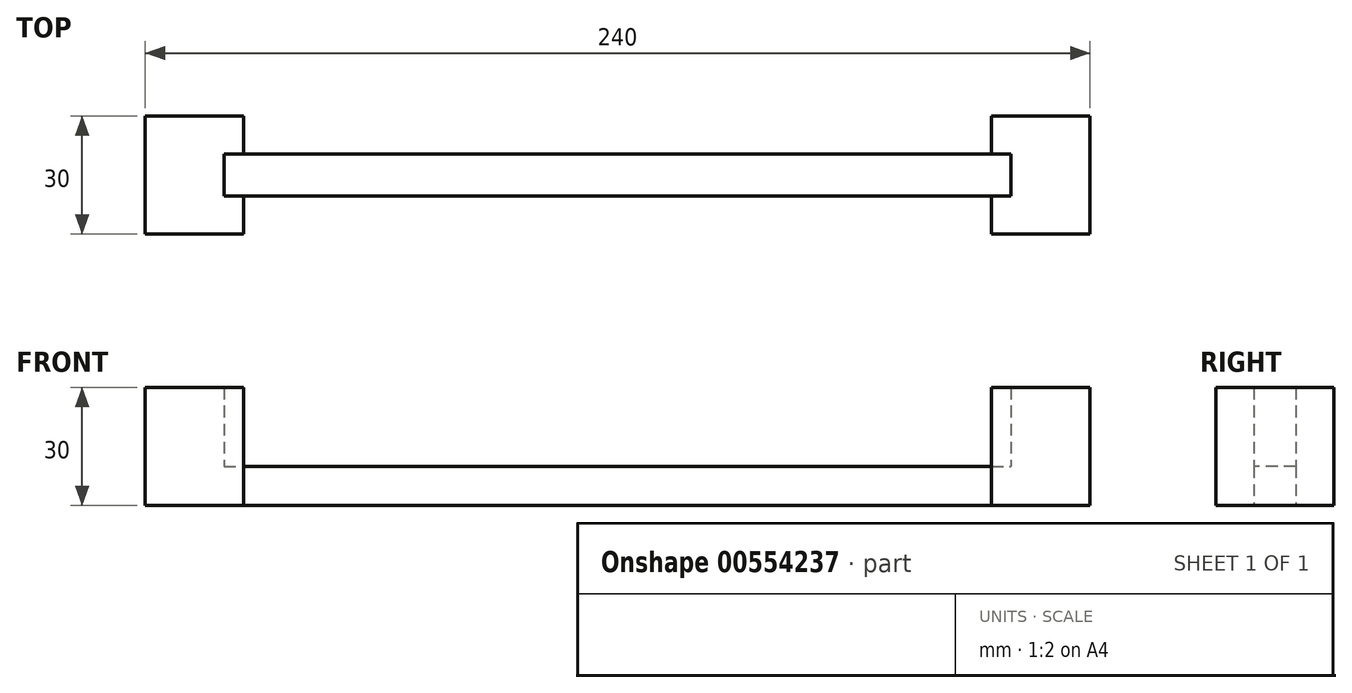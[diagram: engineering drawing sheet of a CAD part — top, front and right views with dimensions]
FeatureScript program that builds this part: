
annotation { "Feature Type Name" : "Feature", "Feature Type Description" : "" }
export const myFeature = defineFeature(function(context is Context, id is Id, definition is map)
    precondition{}
    {
        {
            var Q0;
            Q0=qCreatedBy(makeId("Top.planeOp"),FACE);
            var sketch = newSketch(context, id + "F0", { "sketchPlane" : qUnion([Q0])});
            skLineSegment(sketch, "E0.bottom", {"start": v(-120, 15) * mm, "end": v(120, 15) * mm});
            skLineSegment(sketch, "E0.top", {"start": v(-120, -15) * mm, "end": v(120, -15) * mm});
            skLineSegment(sketch, "E0.left", {"start": v(-120, 15) * mm, "end": v(-120, -15) * mm});
            skLineSegment(sketch, "E0.right", {"start": v(120, 15) * mm, "end": v(120, -15) * mm});
            skPoint(sketch, "E0.middle", {"position": v(0, 0) * mm});
            skLineSegment(sketch, "E1.bottom", {"start": v(100, -5.3) * mm, "end": v(-100, -5.3) * mm});
            skLineSegment(sketch, "E1.top", {"start": v(100, 5.3) * mm, "end": v(-100, 5.3) * mm});
            skLineSegment(sketch, "E1.left", {"start": v(100, -5.3) * mm, "end": v(100, 5.3) * mm});
            skLineSegment(sketch, "E1.right", {"start": v(-100, -5.3) * mm, "end": v(-100, 5.3) * mm});
            skLineSegment(sketch, "E2.bottom", {"start": v(-95, 15) * mm, "end": v(95, 15) * mm});
            skLineSegment(sketch, "E2.top", {"start": v(-95, -15) * mm, "end": v(95, -15) * mm});
            skLineSegment(sketch, "E2.left", {"start": v(-95, 15) * mm, "end": v(-95, -15) * mm});
            skLineSegment(sketch, "E2.right", {"start": v(95, 15) * mm, "end": v(95, -15) * mm});
            skSolve(sketch);
        }
        {
            var Q0;
            {var subQ4=sQuery(id+"F0.wireOp",EDGE,"E0.left");Q0=makeQuery(id+"F0.imprint","IMPRINT",FACE,{"disambiguationData":[TD([[makeQuery(id+"F0.imprint","IMPRINT",EDGE,{"derivedFrom":subQ4}),1.0]])]});}
            var Q1;
            {var subQ5=sQuery(id+"F0.wireOp",EDGE,"E2.bottom");Q1=makeQuery(id+"F0.imprint","IMPRINT",FACE,{"disambiguationData":[TD([[makeQuery(id+"F0.imprint","IMPRINT",EDGE,{"derivedFrom":subQ5}),-1.0]])]});}
            var Q2;
            {var subQ0=sQuery(id+"F0.wireOp",EDGE,"E0.right");Q2=makeQuery(id+"F0.imprint","IMPRINT",FACE,{"disambiguationData":[TD([[makeQuery(id+"F0.imprint","IMPRINT",EDGE,{"derivedFrom":subQ0}),-1.0]])]});}
            var Q3;
            {var subQ5=sQuery(id+"F0.wireOp",EDGE,"E2.top");Q3=makeQuery(id+"F0.imprint","IMPRINT",FACE,{"disambiguationData":[TD([[makeQuery(id+"F0.imprint","IMPRINT",EDGE,{"derivedFrom":subQ5}),1.0]])]});}
            var Q4;
            {var subQ0=sQuery(id+"F0.wireOp",EDGE,"E2.right");var subQ1=sQuery(id+"F0.wireOp",EDGE,"E1.bottom");var subQ2=makeQuery(id+"F0.imprint","INTERSECT",VERTEX,{"derivedFrom":[subQ1,subQ0]});Q4=makeQuery(id+"F0.imprint","IMPRINT",FACE,{"disambiguationData":[TD([[makeQuery(id+"F0.imprint","IMPRINT",EDGE,{"disambiguationData":[TD([[subQ2,-1.0]])],"derivedFrom":subQ1}),-1.0]])]});}
            var Q5;
            {var subQ0=sQuery(id+"F0.wireOp",EDGE,"E1.right");Q5=makeQuery(id+"F0.imprint","IMPRINT",FACE,{"disambiguationData":[TD([[makeQuery(id+"F0.imprint","IMPRINT",EDGE,{"derivedFrom":subQ0}),-1.0]])]});}
            var Q6;
            {var subQ0=sQuery(id+"F0.wireOp",EDGE,"E1.left");Q6=makeQuery(id+"F0.imprint","IMPRINT",FACE,{"disambiguationData":[TD([[makeQuery(id+"F0.imprint","IMPRINT",EDGE,{"derivedFrom":subQ0}),1.0]])]});}
            extrude(context, id + "F1", {"entities" : qUnion([Q0, Q1, Q2, Q3, Q4, Q5, Q6]), "depth" : 10 * mm, "offsetDistance" : 25 * mm});
        }
        {
            var Q0;
            {var subQ4=sQuery(id+"F0.wireOp",EDGE,"E0.left");Q0=makeQuery(id+"F0.imprint","IMPRINT",FACE,{"disambiguationData":[TD([[makeQuery(id+"F0.imprint","IMPRINT",EDGE,{"derivedFrom":subQ4}),1.0]])]});}
            var Q1;
            {var subQ5=sQuery(id+"F0.wireOp",EDGE,"E2.bottom");Q1=makeQuery(id+"F0.imprint","IMPRINT",FACE,{"disambiguationData":[TD([[makeQuery(id+"F0.imprint","IMPRINT",EDGE,{"derivedFrom":subQ5}),-1.0]])]});}
            var Q2;
            {var subQ0=sQuery(id+"F0.wireOp",EDGE,"E0.right");Q2=makeQuery(id+"F0.imprint","IMPRINT",FACE,{"disambiguationData":[TD([[makeQuery(id+"F0.imprint","IMPRINT",EDGE,{"derivedFrom":subQ0}),-1.0]])]});}
            var Q3;
            {var subQ5=sQuery(id+"F0.wireOp",EDGE,"E2.top");Q3=makeQuery(id+"F0.imprint","IMPRINT",FACE,{"disambiguationData":[TD([[makeQuery(id+"F0.imprint","IMPRINT",EDGE,{"derivedFrom":subQ5}),1.0]])]});}
            extrude(context, id + "F2", {"entities" : qUnion([Q0, Q1, Q2, Q3]), "operationType" : NewBodyOperationType.ADD, "depth" : 13 * mm, "offsetDistance" : 25 * mm});
        }
        {
            var Q0;
            {var subQ4=sQuery(id+"F0.wireOp",EDGE,"E0.left");Q0=makeQuery(id+"F0.imprint","IMPRINT",FACE,{"disambiguationData":[TD([[makeQuery(id+"F0.imprint","IMPRINT",EDGE,{"derivedFrom":subQ4}),1.0]])]});}
            var Q1;
            {var subQ0=sQuery(id+"F0.wireOp",EDGE,"E0.right");Q1=makeQuery(id+"F0.imprint","IMPRINT",FACE,{"disambiguationData":[TD([[makeQuery(id+"F0.imprint","IMPRINT",EDGE,{"derivedFrom":subQ0}),-1.0]])]});}
            extrude(context, id + "F3", {"entities" : qUnion([Q0, Q1]), "operationType" : NewBodyOperationType.ADD, "depth" : 30 * mm, "offsetDistance" : 25 * mm});
        }
    });
